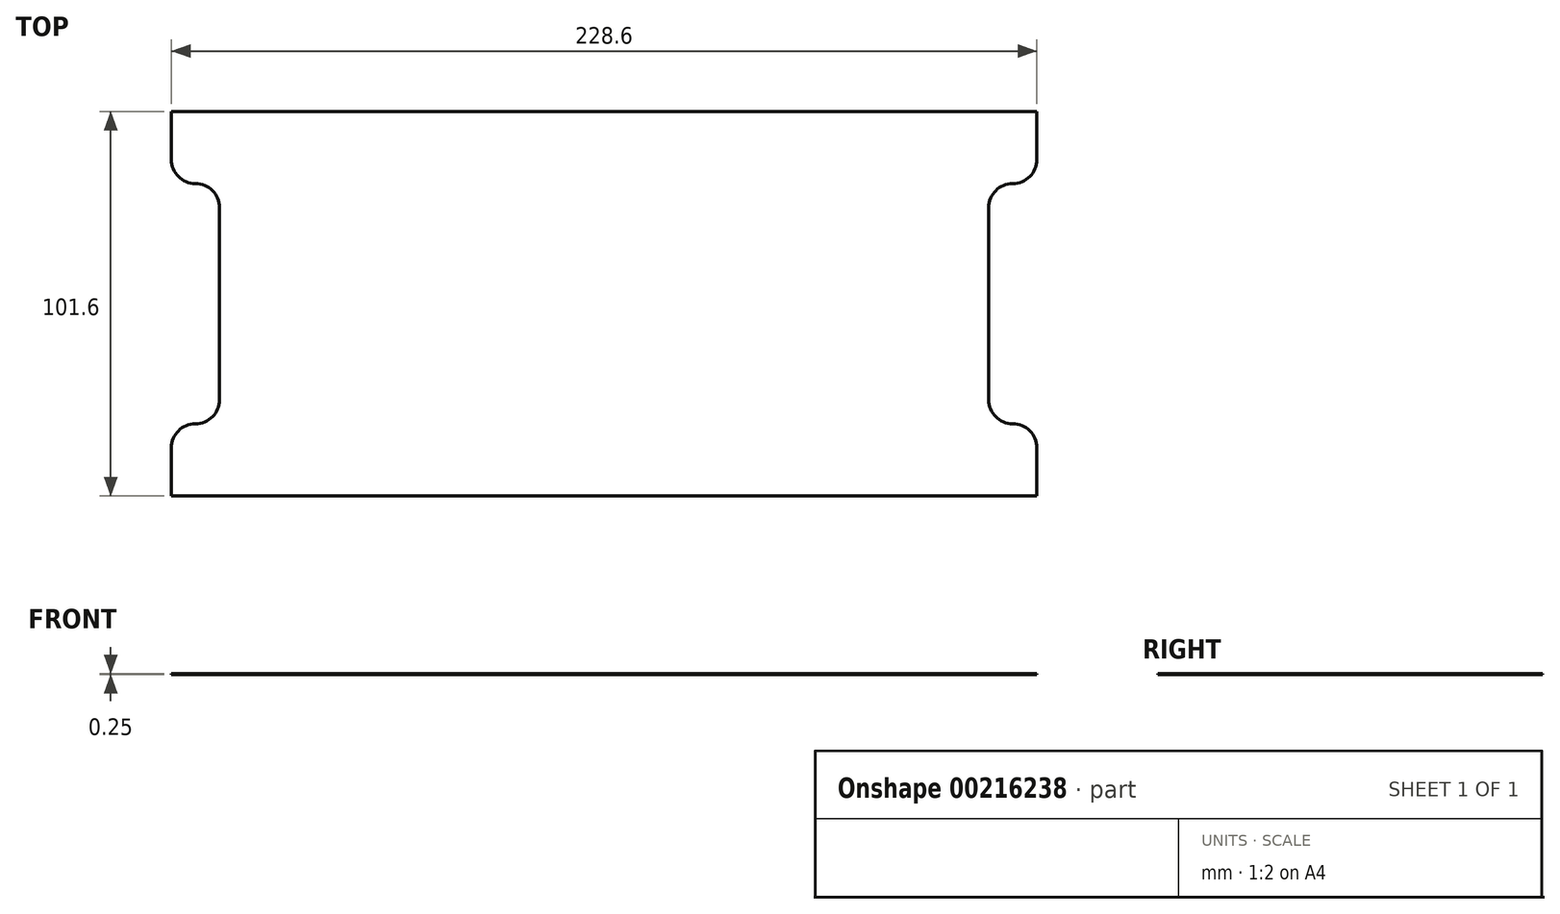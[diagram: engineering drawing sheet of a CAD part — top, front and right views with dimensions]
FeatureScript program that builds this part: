
annotation { "Feature Type Name" : "Feature", "Feature Type Description" : "" }
export const myFeature = defineFeature(function(context is Context, id is Id, definition is map)
    precondition{}
    {
        {
            var Q0;
            Q0=qCreatedBy(makeId("Top.planeOp"),FACE);
            var sketch = newSketch(context, id + "F0", { "sketchPlane" : qUnion([Q0])});
            skLineSegment(sketch, "E0", {"start": v(218.41, 0) * mm, "end": v(-220.34, 0) * mm, "construction": true});
            skLineSegment(sketch, "E1", {"start": v(0, 139.3) * mm, "end": v(0, -144.22) * mm, "construction": true});
            skLineSegment(sketch, "E2", {"start": v(0, 50.8) * mm, "end": v(114.3, 50.8) * mm});
            skLineSegment(sketch, "E3", {"start": v(114.3, 50.8) * mm, "end": v(114.3, 38.1) * mm});
            skArc(sketch, "E4", {"start": v(114.3, 38.1) * mm, "mid": v(112.44, 33.6) * mm, "end": v(107.95, 31.75) * mm});
            skLineSegment(sketch, "E5", {"start": v(101.6, 0) * mm, "end": v(101.6, 25.4) * mm});
            skArc(sketch, "E6", {"start": v(101.6, 25.4) * mm, "mid": v(103.46, 29.9) * mm, "end": v(107.95, 31.75) * mm});
            skLineSegment(sketch, "E7.MirrorCS", {"start": v(-101.6, 0) * mm, "end": v(-101.6, 25.4) * mm});
            skArc(sketch, "E8.MirrorCS", {"start": v(-101.6, 25.4) * mm, "mid": v(-103.46, 29.9) * mm, "end": v(-107.95, 31.75) * mm});
            skArc(sketch, "E9.MirrorCS", {"start": v(-114.3, 38.1) * mm, "mid": v(-112.44, 33.6) * mm, "end": v(-107.95, 31.75) * mm});
            skLineSegment(sketch, "E10.MirrorCS", {"start": v(-114.3, 50.8) * mm, "end": v(-114.3, 38.1) * mm});
            skLineSegment(sketch, "E11.MirrorCS", {"start": v(0, 50.8) * mm, "end": v(-114.3, 50.8) * mm});
            skArc(sketch, "E12.MirrorCS", {"start": v(-101.6, -25.4) * mm, "mid": v(-103.46, -29.9) * mm, "end": v(-107.95, -31.75) * mm});
            skArc(sketch, "E13.MirrorCS", {"start": v(101.6, -25.4) * mm, "mid": v(103.46, -29.9) * mm, "end": v(107.95, -31.75) * mm});
            skLineSegment(sketch, "E14.MirrorCS", {"start": v(114.3, -50.8) * mm, "end": v(114.3, -38.1) * mm});
            skLineSegment(sketch, "E15.MirrorCS", {"start": v(0, -50.8) * mm, "end": v(114.3, -50.8) * mm});
            skArc(sketch, "E16.MirrorCS", {"start": v(114.3, -38.1) * mm, "mid": v(112.44, -33.6) * mm, "end": v(107.95, -31.75) * mm});
            skLineSegment(sketch, "E17.MirrorCS", {"start": v(0, -50.8) * mm, "end": v(-114.3, -50.8) * mm});
            skArc(sketch, "E18.MirrorCS", {"start": v(-114.3, -38.1) * mm, "mid": v(-112.44, -33.6) * mm, "end": v(-107.95, -31.75) * mm});
            skLineSegment(sketch, "E19.MirrorCS", {"start": v(-114.3, -50.8) * mm, "end": v(-114.3, -38.1) * mm});
            skLineSegment(sketch, "E20.MirrorCS", {"start": v(101.6, 0) * mm, "end": v(101.6, -25.4) * mm});
            skLineSegment(sketch, "E21.MirrorCS", {"start": v(-101.6, 0) * mm, "end": v(-101.6, -25.4) * mm});
            skPoint(sketch, "E22", {"position": v(0, 50.8) * mm});
            skPoint(sketch, "E23", {"position": v(63.5, 50.8) * mm});
            skSolve(sketch);
        }
        {
            var Q0;
            Q0 = qSketchRegion(id + "F0", true);
            extrude(context, id + "F1", {"entities" : qUnion([Q0]), "depth" : 0.25 * mm});
        }
    });
